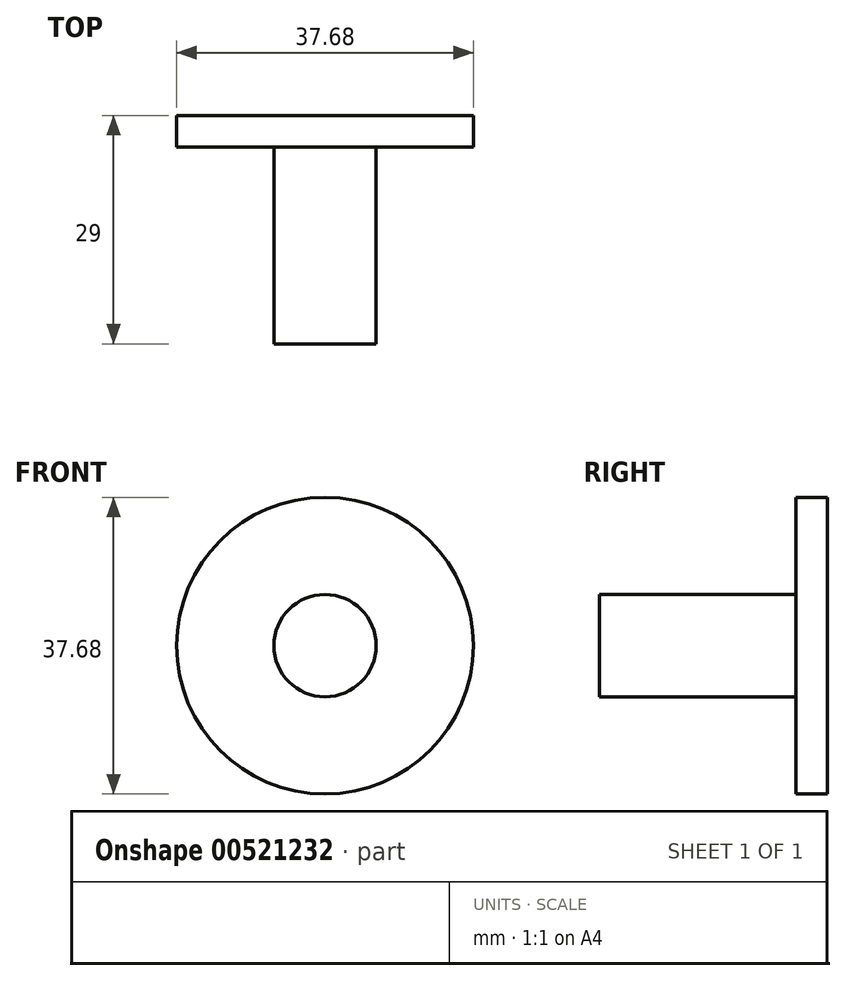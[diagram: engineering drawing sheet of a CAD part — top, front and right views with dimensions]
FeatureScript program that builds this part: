
annotation { "Feature Type Name" : "Feature", "Feature Type Description" : "" }
export const myFeature = defineFeature(function(context is Context, id is Id, definition is map)
    precondition{}
    {
        {
            var Q0;
            Q0=qCreatedBy(makeId("Front.planeOp"),FACE);
            var sketch = newSketch(context, id + "F0", { "sketchPlane" : qUnion([Q0])});
            skCircle(sketch, "E0", {"center": v(0, 0) * mm, "radius": 6.5 * mm});
            skSolve(sketch);
        }
        {
            var Q0;
            Q0=qSketchRegion(id+"F0",true);
            extrude(context, id + "F1", {"entities" : qUnion([Q0]), "depth" : 25 * mm});
        }
        {
            var Q0;
            Q0=makeQuery(id+"F1.opExtrude","CAP_FACE",FACE,{"disambiguationData":[OSD([sQuery(id+"F0.wireOp",EDGE,"E0")])],"isStart":true});
            var sketch = newSketch(context, id + "F2", { "sketchPlane" : qUnion([Q0])});
            skCircle(sketch, "E1", {"center": v(0, 0) * mm, "radius": 18.84 * mm});
            skSolve(sketch);
        }
        {
            var Q0;
            Q0=qSketchRegion(id+"F2",true);
            extrude(context, id + "F3", {"entities" : qUnion([Q0]), "operationType" : NewBodyOperationType.ADD, "depth" : 4 * mm});
        }
    });
